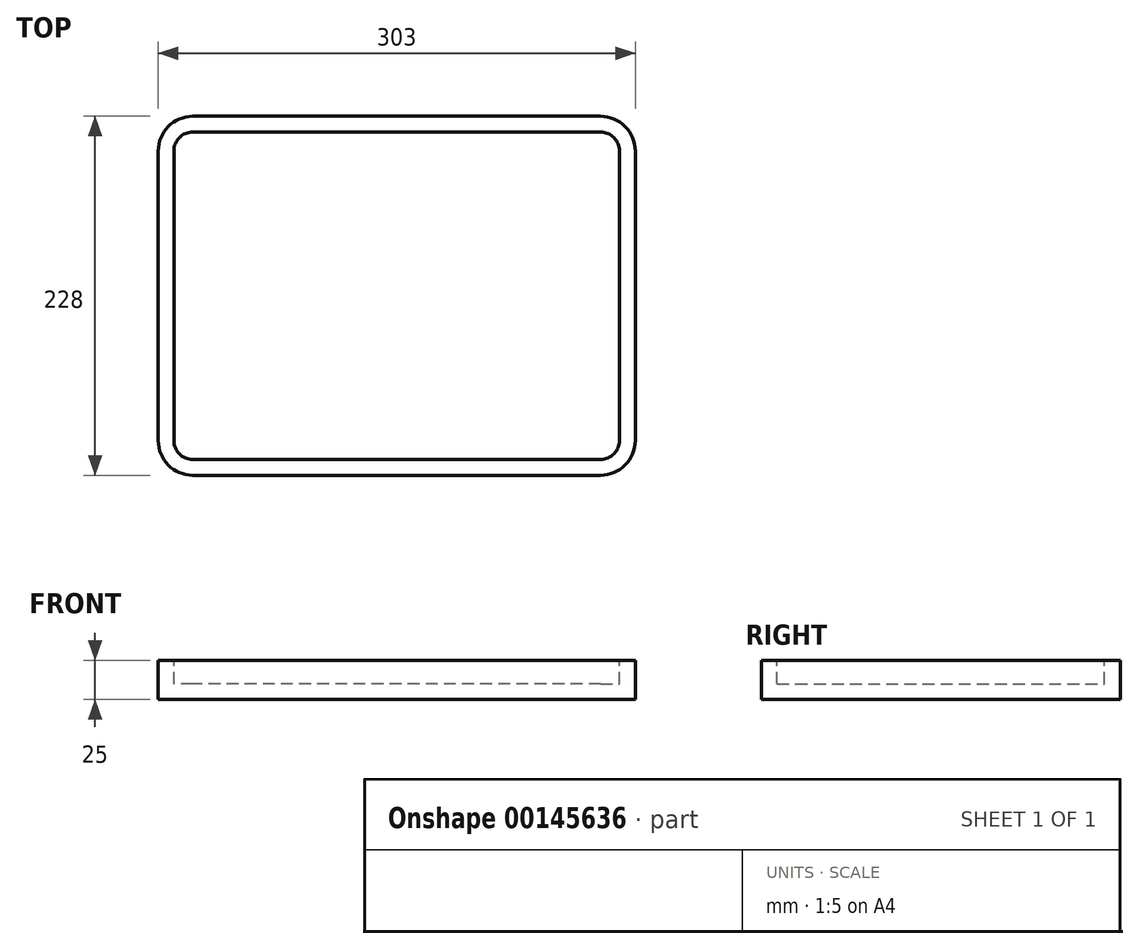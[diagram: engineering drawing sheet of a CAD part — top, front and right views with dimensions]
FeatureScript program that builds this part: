
annotation { "Feature Type Name" : "Feature", "Feature Type Description" : "" }
export const myFeature = defineFeature(function(context is Context, id is Id, definition is map)
    precondition{}
    {
        {
            var Q0;
            Q0=qCreatedBy(makeId("Top.planeOp"),FACE);
            var sketch = newSketch(context, id + "F0", { "sketchPlane" : qUnion([Q0])});
            skLineSegment(sketch, "E0.bottom", {"start": v(129.5, -104) * mm, "end": v(-129.5, -104) * mm});
            skLineSegment(sketch, "E0.top", {"start": v(129.5, 104) * mm, "end": v(-129.5, 104) * mm});
            skLineSegment(sketch, "E0.left", {"start": v(141.5, -92) * mm, "end": v(141.5, 92) * mm});
            skLineSegment(sketch, "E0.right", {"start": v(-141.5, -92) * mm, "end": v(-141.5, 92) * mm});
            skPoint(sketch, "E0.middle", {"position": v(0, 0) * mm});
            skPoint(sketch, "E1.visualSharp", {"position": v(-141.5, -104) * mm});
            skArc(sketch, "E1.filletArc", {"start": v(-141.5, -92) * mm, "mid": v(-137.99, -100.49) * mm, "end": v(-129.5, -104) * mm});
            skPoint(sketch, "E2.visualSharp", {"position": v(141.5, -104) * mm});
            skArc(sketch, "E2.filletArc", {"start": v(129.5, -104) * mm, "mid": v(137.99, -100.49) * mm, "end": v(141.5, -92) * mm});
            skPoint(sketch, "E3.visualSharp", {"position": v(141.5, 104) * mm});
            skArc(sketch, "E3.filletArc", {"start": v(141.5, 92) * mm, "mid": v(137.99, 100.49) * mm, "end": v(129.5, 104) * mm});
            skPoint(sketch, "E4.visualSharp", {"position": v(-141.5, 104) * mm});
            skArc(sketch, "E4.filletArc", {"start": v(-129.5, 104) * mm, "mid": v(-137.99, 100.49) * mm, "end": v(-141.5, 92) * mm});
            skArc(sketch, "E5.0", {"start": v(129.5, -114) * mm, "mid": v(145.06, -107.56) * mm, "end": v(151.5, -92) * mm});
            skLineSegment(sketch, "E5.1", {"start": v(151.5, -92) * mm, "end": v(151.5, 92) * mm});
            skLineSegment(sketch, "E5.2", {"start": v(129.5, -114) * mm, "end": v(-129.5, -114) * mm});
            skArc(sketch, "E5.3", {"start": v(151.5, 92) * mm, "mid": v(145.06, 107.56) * mm, "end": v(129.5, 114) * mm});
            skArc(sketch, "E5.4", {"start": v(-151.5, -92) * mm, "mid": v(-145.06, -107.56) * mm, "end": v(-129.5, -114) * mm});
            skLineSegment(sketch, "E5.5", {"start": v(-151.5, -92) * mm, "end": v(-151.5, 92) * mm});
            skArc(sketch, "E5.6", {"start": v(-129.5, 114) * mm, "mid": v(-145.06, 107.56) * mm, "end": v(-151.5, 92) * mm});
            skLineSegment(sketch, "E5.7", {"start": v(129.5, 114) * mm, "end": v(-129.5, 114) * mm});
            skSolve(sketch);
        }
        {
            var Q0;
            Q0=makeQuery(id+"F0.imprint","IMPRINT",FACE,{"disambiguationData":[TD([[makeQuery(id+"F0.imprint","IMPRINT",EDGE,{"derivedFrom":sQuery(id+"F0.wireOp",EDGE,"E0.bottom")}),-1.0]])]});
            var Q1;
            Q1=makeQuery(id+"F0.imprint","IMPRINT",FACE,{"disambiguationData":[TD([[makeQuery(id+"F0.imprint","IMPRINT",EDGE,{"derivedFrom":sQuery(id+"F0.wireOp",EDGE,"E0.bottom")}),1.0]])]});
            extrude(context, id + "F1", {"entities" : qUnion([Q0, Q1]), "oppositeDirection" : true, "depth" : 25 * mm});
        }
        {
            var Q0;
            Q0=makeQuery(id+"F0.imprint","IMPRINT",FACE,{"disambiguationData":[TD([[makeQuery(id+"F0.imprint","IMPRINT",EDGE,{"derivedFrom":sQuery(id+"F0.wireOp",EDGE,"E0.bottom")}),-1.0]])]});
            extrude(context, id + "F2", {"entities" : qUnion([Q0]), "operationType" : NewBodyOperationType.REMOVE, "oppositeDirection" : true, "depth" : 15 * mm});
        }
    });
